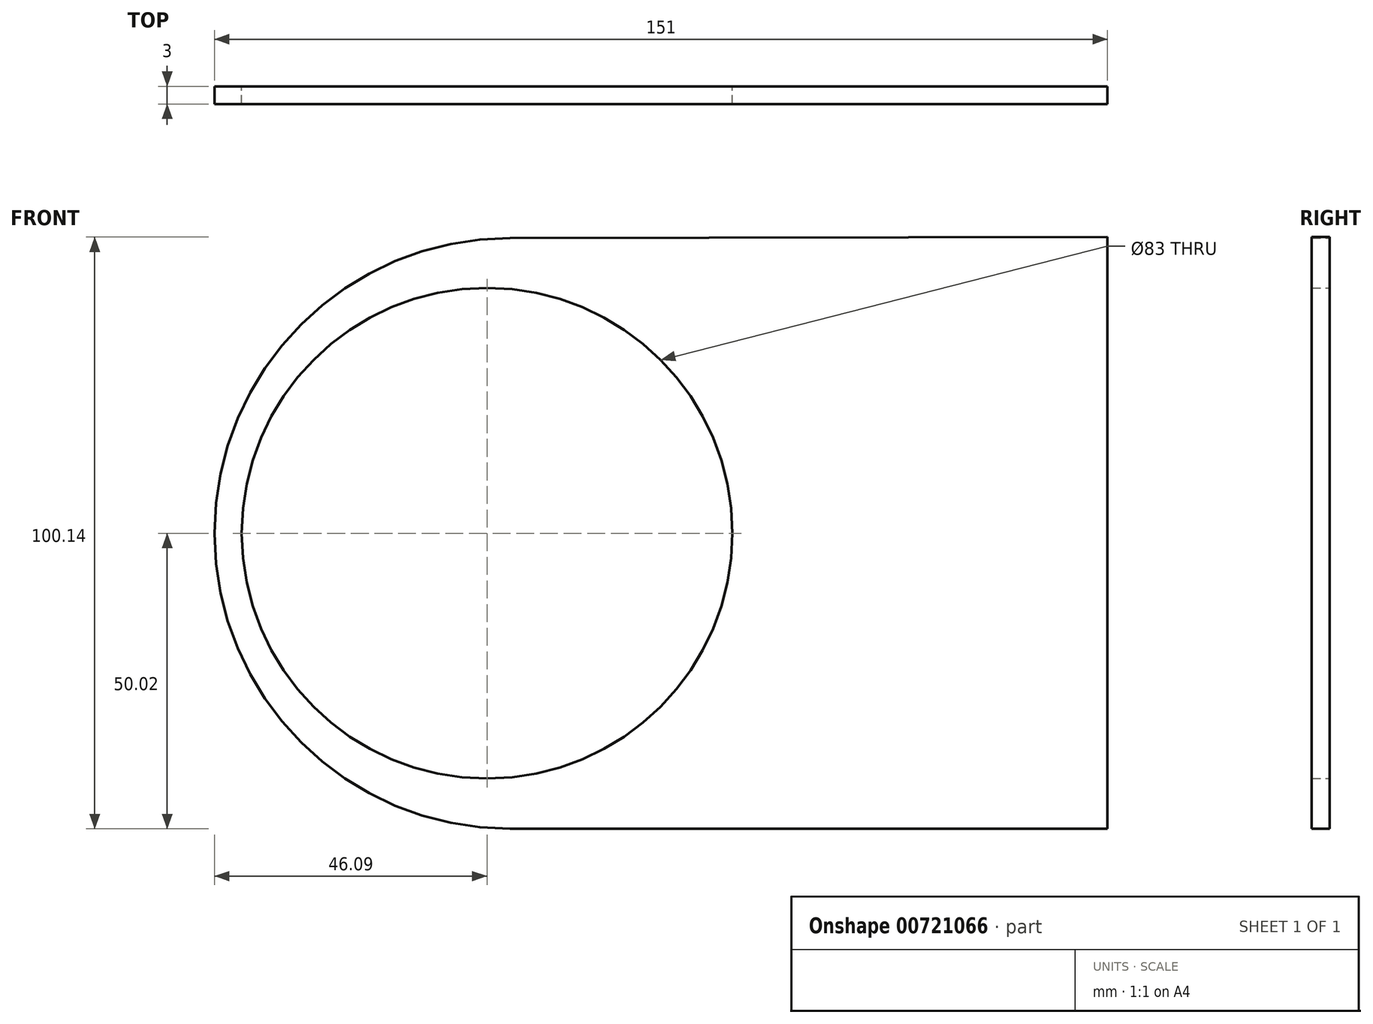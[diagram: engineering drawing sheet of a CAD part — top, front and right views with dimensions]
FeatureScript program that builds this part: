
annotation { "Feature Type Name" : "Feature", "Feature Type Description" : "" }
export const myFeature = defineFeature(function(context is Context, id is Id, definition is map)
    precondition{}
    {
        {
            var Q0;
            Q0=qCreatedBy(makeId("Front.planeOp"),FACE);
            var sketch = newSketch(context, id + "F0", { "sketchPlane" : qUnion([Q0])});
            skArc(sketch, "E0", {"start": v(-122.73, 57.97) * mm, "mid": v(-172.73, 7.97) * mm, "end": v(-122.73, -42.03) * mm});
            skLineSegment(sketch, "E1", {"start": v(-122.73, -42.03) * mm, "end": v(-21.73, -42.03) * mm});
            skLineSegment(sketch, "E2", {"start": v(-21.73, -42.03) * mm, "end": v(-21.73, 57.97) * mm});
            skPoint(sketch, "E3.end.orphan", {"position": v(-172.73, 7.97) * mm});
            skPoint(sketch, "E4.start.orphan", {"position": v(-21.73, 7.97) * mm});
            skLineSegment(sketch, "E5.trimOffspring", {"start": v(-21.73, 57.97) * mm, "end": v(-21.73, 58.11) * mm});
            skPoint(sketch, "E6.end.orphan", {"position": v(-62.73, 92.97) * mm});
            skPoint(sketch, "E7.end.orphan", {"position": v(-62.73, 57.97) * mm});
            skLineSegment(sketch, "E8", {"start": v(-21.73, 58.11) * mm, "end": v(-122.73, 57.97) * mm});
            skSolve(sketch);
        }
        {
            var Q0;
            Q0=qCreatedBy(makeId("Front.planeOp"),FACE);
            var sketch = newSketch(context, id + "F1", { "sketchPlane" : qUnion([Q0])});
            skCircle(sketch, "E9", {"center": v(-126.64, 8) * mm, "radius": 41.5 * mm});
            skCircle(sketch, "E10.0", {"center": v(-126.64, 8) * mm, "radius": 43.1 * mm});
            skSolve(sketch);
        }
        {
            var Q0;
            Q0=qSketchRegion(id+"F0",true);
            extrude(context, id + "F2", {"entities" : qUnion([Q0]), "depth" : 3 * mm, "offsetDistance" : 25 * mm});
        }
        {
            var Q0;
            Q0=sQuery(id+"F1.wireOp",VERTEX,"E9.center");
            var Q1;
            Q1=makeQuery(id+"F2.opExtrude","SWEPT_BODY",BODY,{"disambiguationData":[OSD([sQuery(id+"F0.wireOp",EDGE,"E0"),sQuery(id+"F0.wireOp",EDGE,"E1"),sQuery(id+"F0.wireOp",EDGE,"E2"),sQuery(id+"F0.wireOp",EDGE,"E5.trimOffspring"),sQuery(id+"F0.wireOp",EDGE,"E8")])]});
            hole(context, id + "F3", {"style" : HoleStyle.SIMPLE, "endStyle" : HoleEndStyle.THROUGH, "oppositeDirection" : true, "holeDiameter" : 83 * mm, "majorDiameter" : 5 * mm, "isTappedThrough" : true, "tappedDepth" : 12 * mm, "tapClearance" : 3, "startFromSketch" : true, "locations" : qUnion([Q0]), "scope" : qUnion([Q1])});
        }
    });
